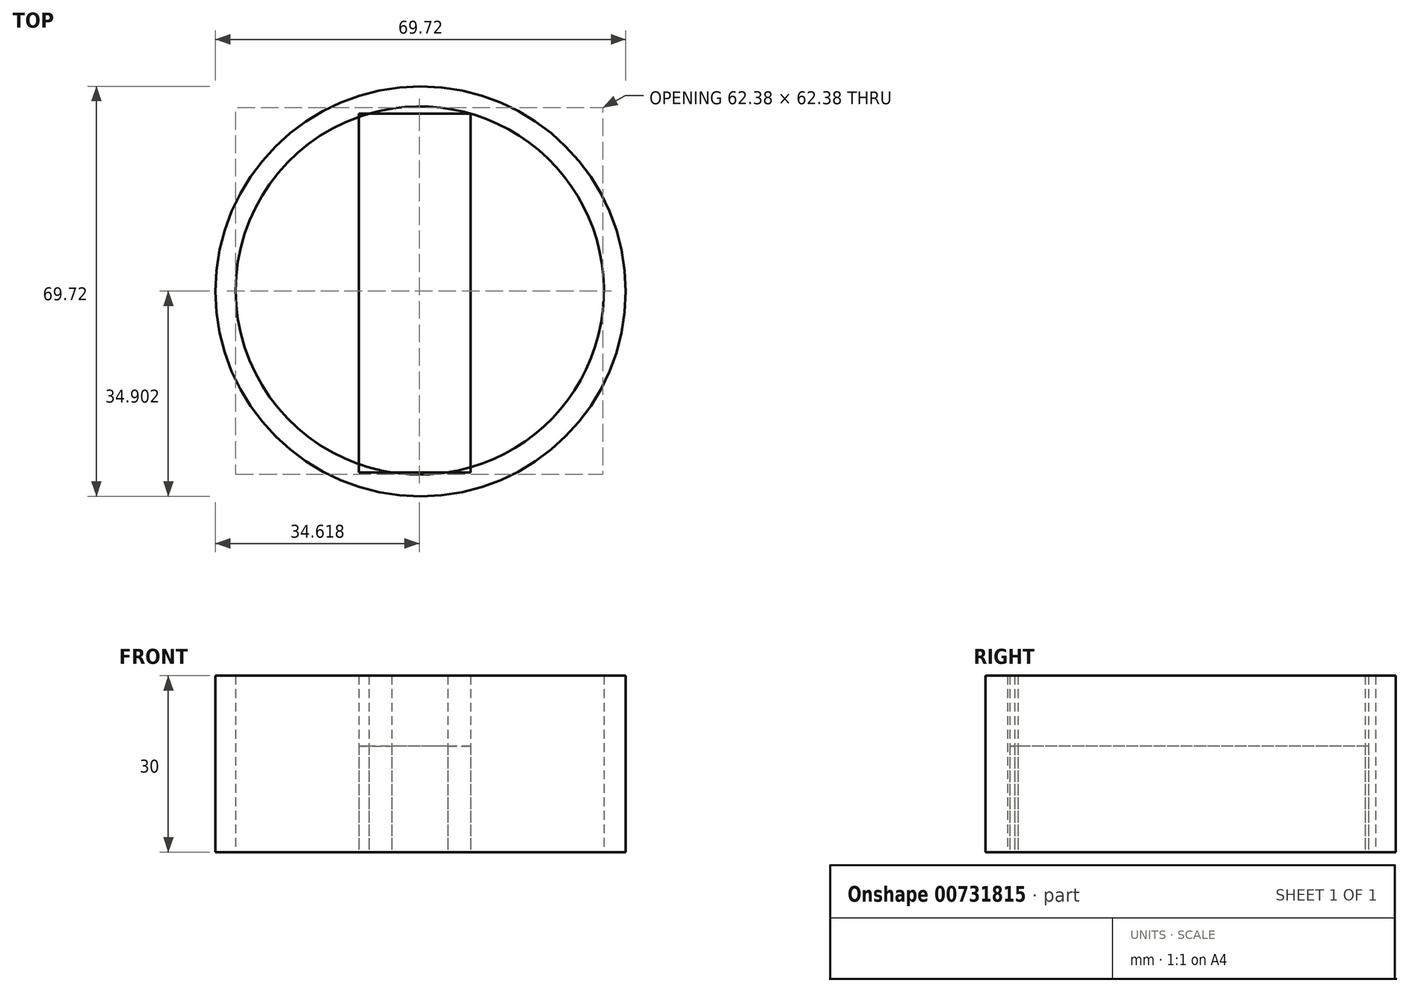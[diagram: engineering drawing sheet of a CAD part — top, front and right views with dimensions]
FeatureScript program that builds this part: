
annotation { "Feature Type Name" : "Feature", "Feature Type Description" : "" }
export const myFeature = defineFeature(function(context is Context, id is Id, definition is map)
    precondition{}
    {
        {
            var Q0;
            Q0=qCreatedBy(makeId("Top.planeOp"),FACE);
            var sketch = newSketch(context, id + "F0", { "sketchPlane" : qUnion([Q0])});
            skLineSegment(sketch, "E0.bottom", {"start": v(8.5, 30.22) * mm, "end": v(-10.5, 30.22) * mm});
            skLineSegment(sketch, "E0.top", {"start": v(8.5, -30.78) * mm, "end": v(-10.5, -30.78) * mm});
            skLineSegment(sketch, "E0.left", {"start": v(8.5, 30.22) * mm, "end": v(8.5, -30.78) * mm});
            skLineSegment(sketch, "E0.right", {"start": v(-10.5, 30.22) * mm, "end": v(-10.5, -30.78) * mm});
            skCircle(sketch, "E1", {"center": v(0, 0) * mm, "radius": 34.86 * mm});
            skCircle(sketch, "E2", {"center": v(-0.14, 0.14) * mm, "radius": 31.29 * mm});
            skSolve(sketch);
        }
        {
            var Q0;
            {var subQ0=sQuery(id+"F0.wireOp",EDGE,"E2");var subQ4=sQuery(id+"F0.wireOp",EDGE,"E0.top");var subQ5=makeQuery(id+"F0.imprint","INTERSECT",VERTEX,{"disambiguationData":[OD(0.0)],"derivedFrom":[subQ4,subQ0]});Q0=makeQuery(id+"F0.imprint","IMPRINT",FACE,{"disambiguationData":[TD([[makeQuery(id+"F0.imprint","IMPRINT",EDGE,{"disambiguationData":[TD([[subQ5,-1.0]])],"derivedFrom":subQ4}),-1.0]])]});}
            extrude(context, id + "F1", {"entities" : qUnion([Q0]), "depth" : 18 * mm, "offsetDistance" : 25 * mm});
        }
        {
            var Q0;
            Q0=makeQuery(id+"F0.imprint","IMPRINT",FACE,{"disambiguationData":[TD([[makeQuery(id+"F0.imprint","IMPRINT",EDGE,{"derivedFrom":sQuery(id+"F0.wireOp",EDGE,"E1")}),1.0]])]});
            extrude(context, id + "F2", {"entities" : qUnion([Q0]), "depth" : 30 * mm, "offsetDistance" : 25 * mm});
        }
    });
